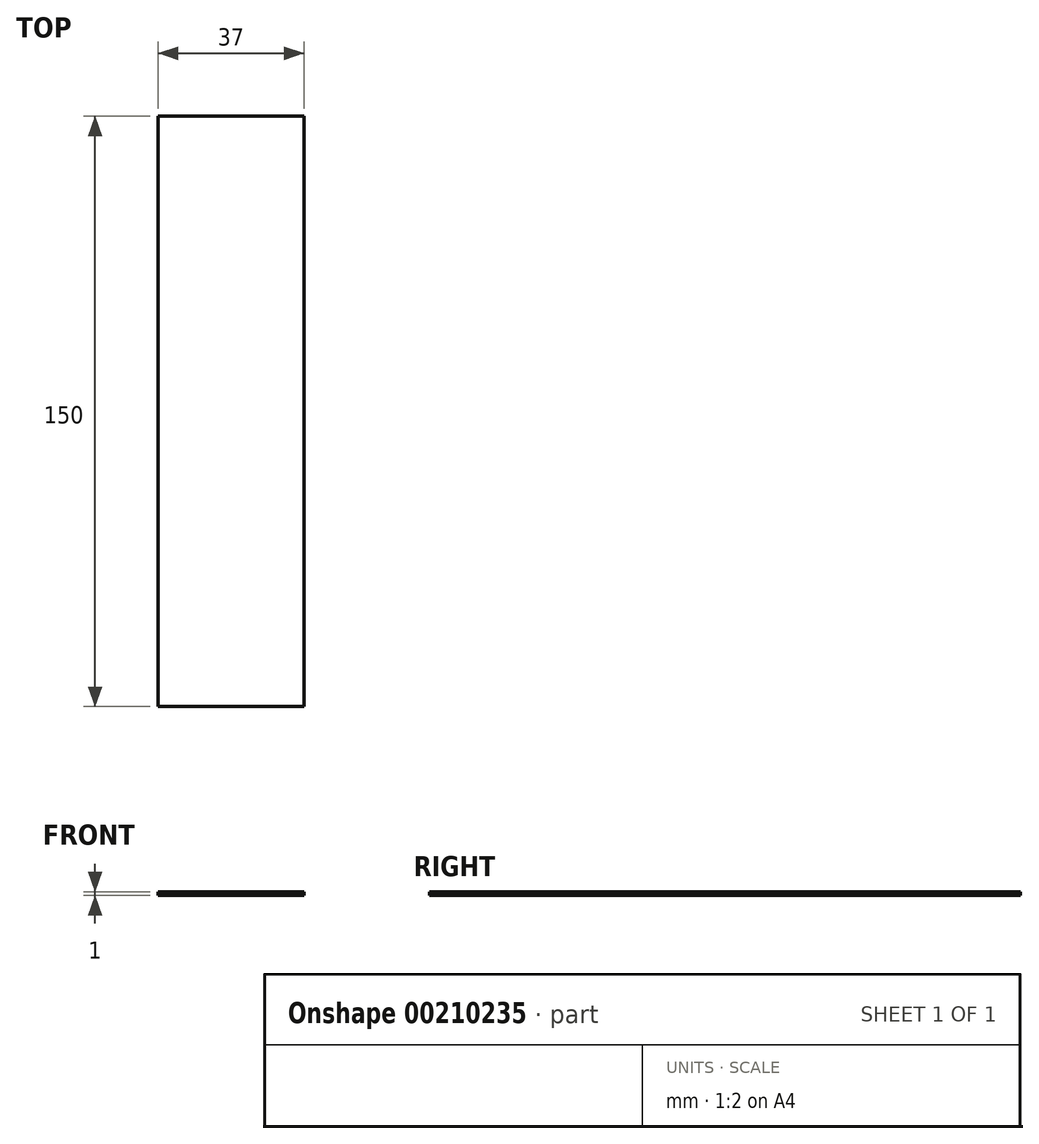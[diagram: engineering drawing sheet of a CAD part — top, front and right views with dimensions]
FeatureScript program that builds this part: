
annotation { "Feature Type Name" : "Feature", "Feature Type Description" : "" }
export const myFeature = defineFeature(function(context is Context, id is Id, definition is map)
    precondition{}
    {
        {
            var Q0;
            Q0=qCreatedBy(makeId("Front.planeOp"),FACE);
            var sketch = newSketch(context, id + "F0", { "sketchPlane" : qUnion([Q0])});
            skLineSegment(sketch, "E0.bottom", {"start": v(-18.5, 0.5) * mm, "end": v(18.5, 0.5) * mm});
            skLineSegment(sketch, "E0.top", {"start": v(-18.5, -0.5) * mm, "end": v(18.5, -0.5) * mm});
            skLineSegment(sketch, "E0.left", {"start": v(-18.5, 0.5) * mm, "end": v(-18.5, -0.5) * mm});
            skLineSegment(sketch, "E0.right", {"start": v(18.5, 0.5) * mm, "end": v(18.5, -0.5) * mm});
            skPoint(sketch, "E0.middle", {"position": v(0, 0) * mm});
            skSolve(sketch);
        }
        {
            var Q0;
            Q0 = qSketchRegion(id + "F0", true);
            extrude(context, id + "F1", {"entities" : qUnion([Q0]), "endBound" : BoundingType.SYMMETRIC, "depth" : 150 * mm});
        }
    });
